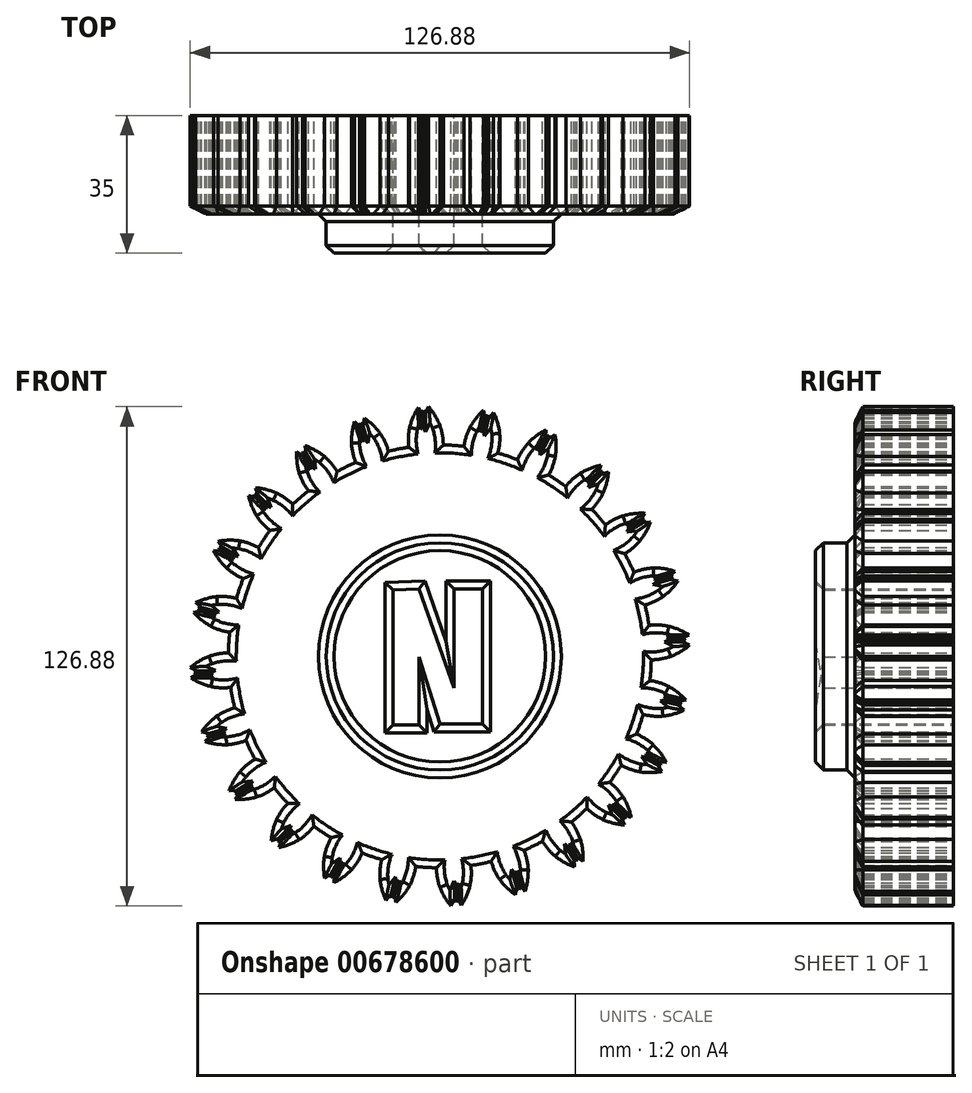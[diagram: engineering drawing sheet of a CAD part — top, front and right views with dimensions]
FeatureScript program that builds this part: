
annotation { "Feature Type Name" : "Feature", "Feature Type Description" : "" }
export const myFeature = defineFeature(function(context is Context, id is Id, definition is map)
    precondition{}
    {
        {
            var Q0;
            Q0=qCreatedBy(makeId("Front.planeOp"),FACE);
            var sketch = newSketch(context, id + "F0", { "sketchPlane" : qUnion([Q0])});
            skCircle(sketch, "E0", {"center": v(0, 0) * mm, "radius": 53.72 * mm});
            skCircle(sketch, "E1", {"center": v(0, 0) * mm, "radius": 58.67 * mm, "construction": true});
            skCircle(sketch, "E2", {"center": v(0, 0) * mm, "radius": 63.5 * mm, "construction": true});
            skLineSegment(sketch, "E3", {"start": v(0, 0) * mm, "end": v(0, 74.65) * mm, "construction": true});
            skLineSegment(sketch, "E4", {"start": v(0, 0) * mm, "end": v(-5.07, 77.35) * mm, "construction": true});
            skCircle(sketch, "E5", {"center": v(0, 58.67) * mm, "radius": 14.6 * mm, "construction": true});
            skLineSegment(sketch, "E6", {"start": v(0, 58.67) * mm, "end": v(-55.85, 58.67) * mm, "construction": true});
            skLineSegment(sketch, "E7", {"start": v(0, 58.67) * mm, "end": v(-55.84, 38.35) * mm, "construction": true});
            skCircle(sketch, "E8", {"center": v(-13.72, 53.68) * mm, "radius": 14.6 * mm, "construction": true});
            skArc(sketch, "E9", {"start": v(0, 58.67) * mm, "mid": v(-1.23, 61.18) * mm, "end": v(-2.86, 63.44) * mm});
            skArc(sketch, "E10", {"start": v(0.88, 53.71) * mm, "mid": v(0.65, 56.23) * mm, "end": v(0, 58.67) * mm});
            skArc(sketch, "E11.MirrorCS", {"start": v(-7.66, 58.17) * mm, "mid": v(-6.77, 60.81) * mm, "end": v(-5.45, 63.27) * mm});
            skArc(sketch, "E12.MirrorCS", {"start": v(-7.88, 53.14) * mm, "mid": v(-7.98, 55.67) * mm, "end": v(-7.66, 58.17) * mm});
            skLineSegment(sketch, "E13", {"start": v(-5.45, 63.27) * mm, "end": v(-4.63, 61.64) * mm});
            skLineSegment(sketch, "E14", {"start": v(-4.63, 61.64) * mm, "end": v(-4.1, 62.45) * mm});
            skPoint(sketch, "E14.endSnap0", {"position": v(-5.04, 62.45) * mm});
            skLineSegment(sketch, "E15", {"start": v(-4.1, 62.45) * mm, "end": v(-3.68, 61.64) * mm});
            skLineSegment(sketch, "E16", {"start": v(-3.68, 61.64) * mm, "end": v(-2.86, 63.44) * mm});
            skCircle(sketch, "E17", {"center": v(0, 0) * mm, "radius": 28.87 * mm});
            skLineSegment(sketch, "E18", {"start": v(-11.94, 16.88) * mm, "end": v(-11.94, -17.48) * mm});
            skLineSegment(sketch, "E19", {"start": v(-11.94, -17.48) * mm, "end": v(-5.23, -17.48) * mm});
            skLineSegment(sketch, "E20", {"start": v(-5.23, -17.48) * mm, "end": v(-5.23, -0.2) * mm});
            skLineSegment(sketch, "E21", {"start": v(-5.23, -0.2) * mm, "end": v(0, -17.2) * mm});
            skLineSegment(sketch, "E22", {"start": v(0, -17.2) * mm, "end": v(10.87, -17.2) * mm});
            skLineSegment(sketch, "E23", {"start": v(10.87, -17.2) * mm, "end": v(10.87, 17.15) * mm});
            skLineSegment(sketch, "E24", {"start": v(10.87, 17.15) * mm, "end": v(3.54, 17.15) * mm});
            skLineSegment(sketch, "E25", {"start": v(3.54, 17.15) * mm, "end": v(3.54, -8.04) * mm});
            skLineSegment(sketch, "E26", {"start": v(3.54, -8.04) * mm, "end": v(-5.23, 17.15) * mm});
            skLineSegment(sketch, "E27", {"start": v(-5.23, 17.15) * mm, "end": v(-11.94, 16.88) * mm});
            skSolve(sketch);
        }
        {
            var Q0;
            Q0=makeQuery(id+"F0.imprint","IMPRINT",FACE,{"disambiguationData":[TD([[makeQuery(id+"F0.imprint","IMPRINT",EDGE,{"derivedFrom":sQuery(id+"F0.wireOp",EDGE,"E9")}),1.0]])]});
            var Q1;
            {var subQ0=sQuery(id+"F0.wireOp",EDGE,"E0");var subQ1=makeQuery(id+"F0.imprint","INTERSECT",VERTEX,{"derivedFrom":[subQ0,sQuery(id+"F0.wireOp",EDGE,"E10")]});Q1=makeQuery(id+"F0.imprint","IMPRINT",FACE,{"disambiguationData":[TD([[makeQuery(id+"F0.imprint","IMPRINT",EDGE,{"disambiguationData":[TD([[subQ1,-1.0]])],"derivedFrom":subQ0}),1.0]])]});}
            extrude(context, id + "F1", {"entities" : qUnion([Q0, Q1]), "depth" : 25 * mm, "offsetDistance" : 25 * mm});
        }
        {
            var Q0;
            Q0=makeQuery(id+"F1.opExtrude","SWEPT_BODY",BODY,{"disambiguationData":[OSD([sQuery(id+"F0.wireOp",EDGE,"E0"),sQuery(id+"F0.wireOp",EDGE,"E9"),sQuery(id+"F0.wireOp",EDGE,"E10"),sQuery(id+"F0.wireOp",EDGE,"E11.MirrorCS"),sQuery(id+"F0.wireOp",EDGE,"E12.MirrorCS"),sQuery(id+"F0.wireOp",EDGE,"E13"),sQuery(id+"F0.wireOp",EDGE,"E14"),sQuery(id+"F0.wireOp",EDGE,"E15"),sQuery(id+"F0.wireOp",EDGE,"E16")])]});
            var Q1;
            Q1=makeQuery(id+"F1.opExtrude","SWEPT_FACE",FACE,{"disambiguationData":[OSD([sQuery(id+"F0.wireOp",EDGE,"E0")])]});
            circularPattern(context, id + "F2", {"entities" : qUnion([Q0]), "axis" : qUnion([Q1]), "angle" : 360 * degree, "instanceCount" : 24, "equalSpace" : true});
        }
        {
            var Q0;
            Q0=makeQuery(id+"F0.imprint","IMPRINT",FACE,{"disambiguationData":[TD([[makeQuery(id+"F0.imprint","IMPRINT",EDGE,{"derivedFrom":sQuery(id+"F0.wireOp",EDGE,"E17")}),1.0]])]});
            extrude(context, id + "F3", {"entities" : qUnion([Q0]), "operationType" : NewBodyOperationType.ADD, "depth" : 35 * mm, "offsetDistance" : 25 * mm});
        }
        {
            var Q0;
            {var subQ0=makeQuery(id+"F1.opExtrude","CAP_FACE",FACE,{"disambiguationData":[OSD([sQuery(id+"F0.wireOp",EDGE,"E0"),sQuery(id+"F0.wireOp",EDGE,"E9"),sQuery(id+"F0.wireOp",EDGE,"E10"),sQuery(id+"F0.wireOp",EDGE,"E11.MirrorCS"),sQuery(id+"F0.wireOp",EDGE,"E12.MirrorCS"),sQuery(id+"F0.wireOp",EDGE,"E13"),sQuery(id+"F0.wireOp",EDGE,"E14"),sQuery(id+"F0.wireOp",EDGE,"E15"),sQuery(id+"F0.wireOp",EDGE,"E16"),sQuery(id+"F0.wireOp",EDGE,"E17")])],"isStart":false});Q0=makeQuery(id+"F3.boolean.opBoolean","MERGE",FACE,{"derivedFrom":[subQ0,makeQuery(id+"F2.opPattern","COPY",FACE,{"derivedFrom":subQ0,"instanceName":"1"}),makeQuery(id+"F2.opPattern","COPY",FACE,{"derivedFrom":subQ0,"instanceName":"2"}),makeQuery(id+"F2.opPattern","COPY",FACE,{"derivedFrom":subQ0,"instanceName":"3"}),makeQuery(id+"F2.opPattern","COPY",FACE,{"derivedFrom":subQ0,"instanceName":"4"}),makeQuery(id+"F2.opPattern","COPY",FACE,{"derivedFrom":subQ0,"instanceName":"5"}),makeQuery(id+"F2.opPattern","COPY",FACE,{"derivedFrom":subQ0,"instanceName":"6"}),makeQuery(id+"F2.opPattern","COPY",FACE,{"derivedFrom":subQ0,"instanceName":"7"}),makeQuery(id+"F2.opPattern","COPY",FACE,{"derivedFrom":subQ0,"instanceName":"8"}),makeQuery(id+"F2.opPattern","COPY",FACE,{"derivedFrom":subQ0,"instanceName":"9"}),makeQuery(id+"F2.opPattern","COPY",FACE,{"derivedFrom":subQ0,"instanceName":"10"}),makeQuery(id+"F2.opPattern","COPY",FACE,{"derivedFrom":subQ0,"instanceName":"11"}),makeQuery(id+"F2.opPattern","COPY",FACE,{"derivedFrom":subQ0,"instanceName":"12"}),makeQuery(id+"F2.opPattern","COPY",FACE,{"derivedFrom":subQ0,"instanceName":"13"}),makeQuery(id+"F2.opPattern","COPY",FACE,{"derivedFrom":subQ0,"instanceName":"14"}),makeQuery(id+"F2.opPattern","COPY",FACE,{"derivedFrom":subQ0,"instanceName":"15"}),makeQuery(id+"F2.opPattern","COPY",FACE,{"derivedFrom":subQ0,"instanceName":"16"}),makeQuery(id+"F2.opPattern","COPY",FACE,{"derivedFrom":subQ0,"instanceName":"17"}),makeQuery(id+"F2.opPattern","COPY",FACE,{"derivedFrom":subQ0,"instanceName":"18"}),makeQuery(id+"F2.opPattern","COPY",FACE,{"derivedFrom":subQ0,"instanceName":"19"}),makeQuery(id+"F2.opPattern","COPY",FACE,{"derivedFrom":subQ0,"instanceName":"20"}),makeQuery(id+"F2.opPattern","COPY",FACE,{"derivedFrom":subQ0,"instanceName":"21"}),makeQuery(id+"F2.opPattern","COPY",FACE,{"derivedFrom":subQ0,"instanceName":"22"}),makeQuery(id+"F2.opPattern","COPY",FACE,{"derivedFrom":subQ0,"instanceName":"23"})]});}
            var Q1;
            Q1=makeQuery(id+"F3.opExtrude","SWEPT_FACE",FACE,{"disambiguationData":[OSD([sQuery(id+"F0.wireOp",EDGE,"E17")])]});
            var Q2;
            Q2=makeQuery(id+"F3.opExtrude","CAP_FACE",FACE,{"disambiguationData":[OSD([sQuery(id+"F0.wireOp",EDGE,"E17"),sQuery(id+"F0.wireOp",EDGE,"E18"),sQuery(id+"F0.wireOp",EDGE,"E19"),sQuery(id+"F0.wireOp",EDGE,"E20"),sQuery(id+"F0.wireOp",EDGE,"E21"),sQuery(id+"F0.wireOp",EDGE,"E22"),sQuery(id+"F0.wireOp",EDGE,"E23"),sQuery(id+"F0.wireOp",EDGE,"E24"),sQuery(id+"F0.wireOp",EDGE,"E25"),sQuery(id+"F0.wireOp",EDGE,"E26"),sQuery(id+"F0.wireOp",EDGE,"E27")])],"isStart":false});
            chamfer(context, id + "F4", {"entities" : qUnion([Q0, Q1, Q2]), "width" : 2 * mm, "tangentPropagation" : true});
        }
    });
